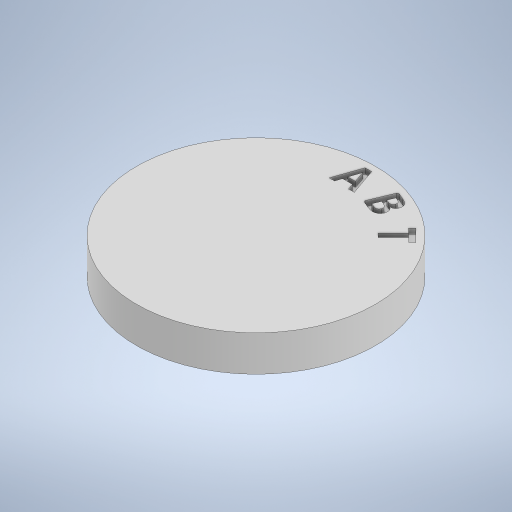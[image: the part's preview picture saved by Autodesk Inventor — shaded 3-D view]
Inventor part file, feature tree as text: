
AUTODESK INVENTOR PART (.ipt)
format: ipt  version: 2023 (Build 270158000, 158)  size: 294,400 bytes
history: native  units: mm
features: extrude x3, sketch x3
ambient origin geometry x8: Origin, YZ Plane, XZ Plane, XY Plane, X Axis, Y Axis, Z Axis, Center Point
bodies: 实体1 (feature_tree)
feature tree (6):
  extrude  "拉伸1"  Depth=2.1mm
  extrude  "拉伸2"  Depth=2.3mm TaperAngle=0.0deg
  extrude  "拉伸3"  Depth=18.0mm
  sketch  "草图1"  dims[d0=3.0mm d1=2.1mm]
  sketch  "草图2"  dims[d2=18.0mm d3=2.3mm d4=0.0mm]
  sketch  "草图3"  dims[d5=0.4mm d6=0.0mm d7=18.0mm d12=0.4mm d13=0.0mm d15=160.0mm d17=360.0deg d19=6.5mm d20=6.5mm d21=6.5mm]
